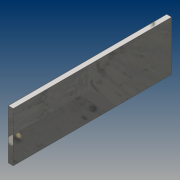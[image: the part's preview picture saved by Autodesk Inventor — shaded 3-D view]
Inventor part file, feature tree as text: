
AUTODESK INVENTOR PART (.ipt)
format: ipt  version: 2021 (Build 250183000, 183)  size: 94,208 bytes
history: native  units: mm
features: extrude x1, sketch x1
ambient origin geometry x8: Origin, YZ Plane, XZ Plane, XY Plane, X Axis, Y Axis, Z Axis, Center Point
bodies: Solid1 (feature_tree)
feature tree (2):
  extrude  "Extrusion1"  Depth=100.0mm
  sketch  "Sketch1"  dims[d0=320.0mm d1=100.0mm d2=10.0mm d3=0.0mm]
